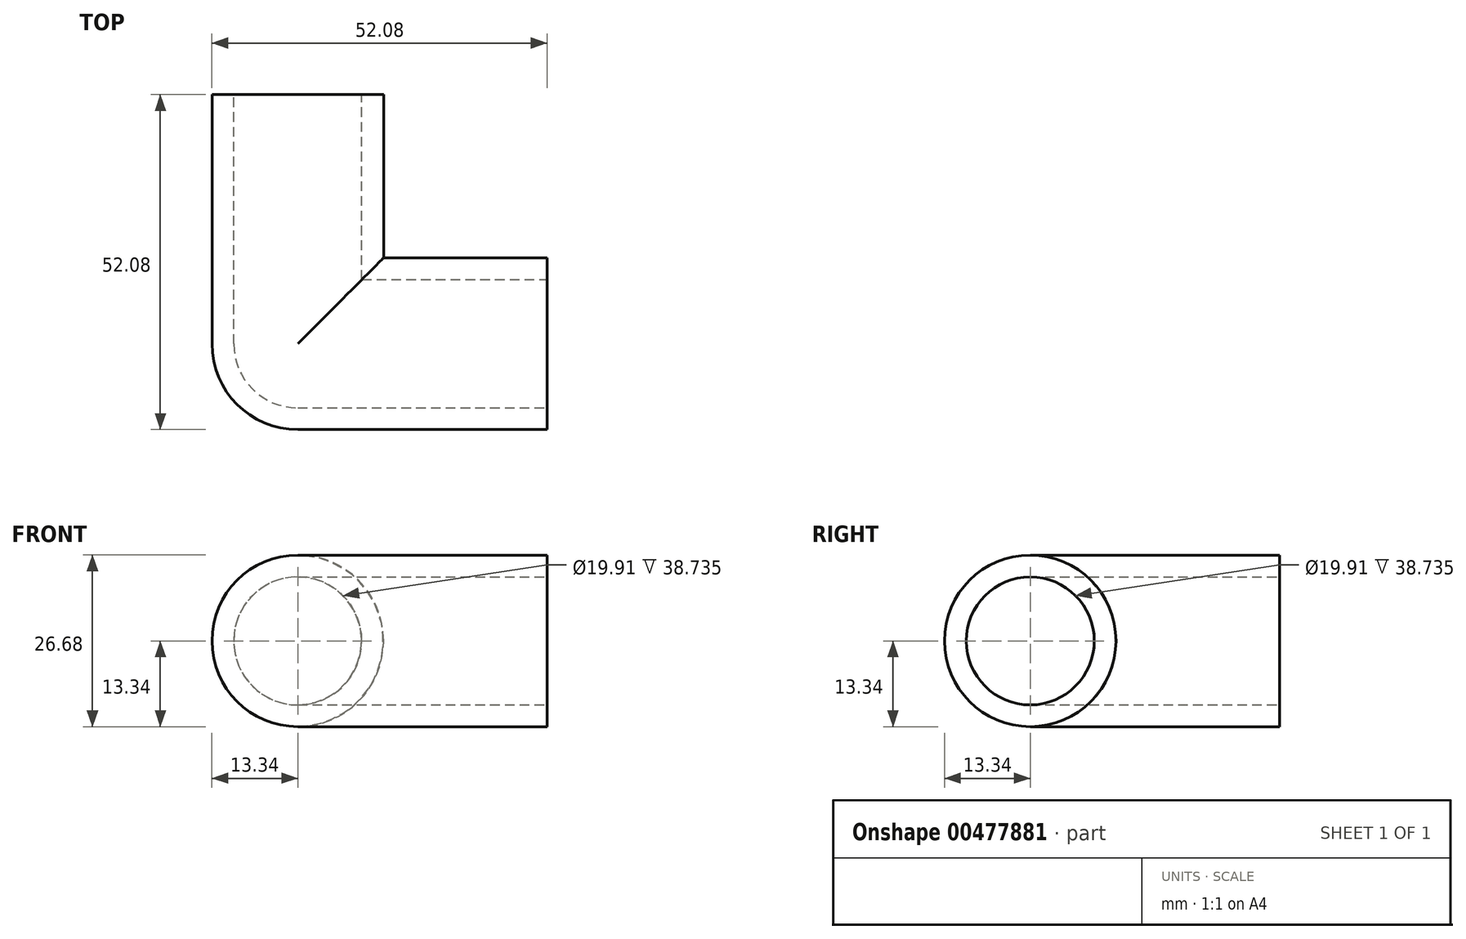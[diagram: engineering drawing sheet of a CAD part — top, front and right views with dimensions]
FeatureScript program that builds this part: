
annotation { "Feature Type Name" : "Feature", "Feature Type Description" : "" }
export const myFeature = defineFeature(function(context is Context, id is Id, definition is map)
    precondition{}
    {
        {
            var Q0;
            Q0=qCreatedBy(makeId("Top.planeOp"),FACE);
            var sketch = newSketch(context, id + "F0", { "sketchPlane" : qUnion([Q0])});
            skLineSegment(sketch, "E0", {"start": v(38.74, 13.33) * mm, "end": v(38.74, -13.33) * mm});
            skLineSegment(sketch, "E1", {"start": v(38.74, -13.34) * mm, "end": v(9.96, -13.34) * mm});
            skLineSegment(sketch, "E2", {"start": v(38.74, -9.96) * mm, "end": v(9.96, -9.96) * mm});
            skLineSegment(sketch, "E3", {"start": v(38.74, 13.33) * mm, "end": v(13.34, 13.33) * mm});
            skLineSegment(sketch, "E4", {"start": v(38.74, 9.96) * mm, "end": v(13.33, 9.96) * mm, "construction": true});
            skLineSegment(sketch, "E5", {"start": v(13.34, 38.73) * mm, "end": v(-13.33, 38.73) * mm});
            skLineSegment(sketch, "E6", {"start": v(-13.33, 38.73) * mm, "end": v(-13.33, 13.33) * mm});
            skLineSegment(sketch, "E7", {"start": v(-9.96, 38.73) * mm, "end": v(-9.96, 13.33) * mm});
            skLineSegment(sketch, "E8", {"start": v(9.96, 38.73) * mm, "end": v(9.96, 13.33) * mm, "construction": true});
            skLineSegment(sketch, "E9", {"start": v(13.34, 38.73) * mm, "end": v(13.34, 13.33) * mm});
            skLineSegment(sketch, "E10", {"start": v(26.04, 13.33) * mm, "end": v(26.03, 9.96) * mm, "construction": true});
            skLineSegment(sketch, "E11", {"start": v(24.35, -9.96) * mm, "end": v(24.35, -13.34) * mm, "construction": true});
            skLineSegment(sketch, "E12", {"start": v(-13.33, 26.03) * mm, "end": v(-9.96, 26.03) * mm, "construction": true});
            skPoint(sketch, "E12.startSnap0", {"position": v(-13.33, 26.03) * mm});
            skLineSegment(sketch, "E13", {"start": v(9.96, 26.03) * mm, "end": v(13.34, 26.03) * mm, "construction": true});
            skArc(sketch, "E14", {"start": v(13.33, 9.96) * mm, "mid": v(10.95, 10.95) * mm, "end": v(9.96, 13.33) * mm, "construction": true});
            skLineSegment(sketch, "E15", {"start": v(9.96, -13.34) * mm, "end": v(0, -13.34) * mm});
            skLineSegment(sketch, "E16", {"start": v(-13.33, 0) * mm, "end": v(-13.33, 13.33) * mm});
            skLineSegment(sketch, "E17", {"start": v(-9.96, 13.33) * mm, "end": v(-9.96, 0) * mm});
            skLineSegment(sketch, "E18", {"start": v(0, -9.96) * mm, "end": v(9.96, -9.96) * mm});
            skLineSegment(sketch, "E19", {"start": v(38.74, 0) * mm, "end": v(-9.96, 0) * mm});
            skPoint(sketch, "E19.endSnap0", {"position": v(-9.96, 1.69) * mm});
            skLineSegment(sketch, "E20", {"start": v(0, 38.73) * mm, "end": v(0, -9.96) * mm});
            skLineSegment(sketch, "E21", {"start": v(-9.96, 0) * mm, "end": v(-13.33, 0) * mm});
            skLineSegment(sketch, "E22", {"start": v(0, -9.96) * mm, "end": v(0, -13.34) * mm});
            skPoint(sketch, "E23", {"position": v(0, 0) * mm});
            skPoint(sketch, "E24.orphan", {"position": v(-13.33, -13.33) * mm});
            skPoint(sketch, "E25.start.orphan", {"position": v(-9.96, -9.96) * mm});
            skSolve(sketch);
        }
        {
            var Q0;
            {var subQ2=sQuery(id+"F0.wireOp",EDGE,"E1");Q0=makeQuery(id+"F0.imprint","IMPRINT",FACE,{"disambiguationData":[TD([[makeQuery(id+"F0.imprint","IMPRINT",EDGE,{"derivedFrom":subQ2}),-1.0]])]});}
            var Q1;
            Q1=sQuery(id+"F0.wireOp",EDGE,"E19");
            revolve(context, id + "F1", {"entities" : qUnion([Q0]), "axis" : qUnion([Q1]), "revolveType" : RevolveType.FULL});
        }
        {
            var Q0;
            {var subQ1=sQuery(id+"F0.wireOp",EDGE,"E6");Q0=makeQuery(id+"F0.imprint","IMPRINT",FACE,{"disambiguationData":[TD([[makeQuery(id+"F0.imprint","IMPRINT",EDGE,{"derivedFrom":subQ1}),1.0]])]});}
            var Q1;
            Q1=sQuery(id+"F0.wireOp",EDGE,"E20");
            revolve(context, id + "F2", {"operationType" : NewBodyOperationType.ADD, "entities" : qUnion([Q0]), "axis" : qUnion([Q1]), "revolveType" : RevolveType.FULL});
        }
        {
            var Q0;
            Q0=makeQuery(id+"F1.opRevolve","SWEPT_FACE",FACE,{"disambiguationData":[OSD([sQuery(id+"F0.wireOp",EDGE,"E0")])]});
            var sketch = newSketch(context, id + "F3", { "sketchPlane" : qUnion([Q0])});
            skSolve(sketch);
        }
        {
            var Q0;
            Q0=makeQuery(id+"F3.imprint","IMPRINT",FACE,{"disambiguationData":[TD([[makeQuery(id+"F3.imprint","IMPRINT",EDGE,{"derivedFrom":makeQuery(id+"F1.opRevolve","SWEPT_EDGE",EDGE,{"disambiguationData":[OSD([sQuery(id+"F0.wireOp",EDGE,"E0"),sQuery(id+"F0.wireOp",EDGE,"E2")])]})}),1.0]])]});
            var Q1;
            Q1=sQuery(id+"F0.wireOp",VERTEX,"E23");
            extrude(context, id + "F4", {"entities" : qUnion([Q0]), "operationType" : NewBodyOperationType.REMOVE, "endBound" : BoundingType.UP_TO_VERTEX, "oppositeDirection" : true, "endBoundEntityVertex" : qUnion([Q1]), "depth" : 25.4 * mm});
        }
        {
            var Q0;
            Q0=makeQuery(id+"F2.opRevolve","SWEPT_FACE",FACE,{"disambiguationData":[OSD([sQuery(id+"F0.wireOp",EDGE,"E5")])]});
            var sketch = newSketch(context, id + "F5", { "sketchPlane" : qUnion([Q0])});
            skSolve(sketch);
        }
        {
            var Q0;
            Q0=makeQuery(id+"F5.imprint","IMPRINT",FACE,{"disambiguationData":[TD([[makeQuery(id+"F5.imprint","IMPRINT",EDGE,{"derivedFrom":makeQuery(id+"F2.opRevolve","SWEPT_EDGE",EDGE,{"disambiguationData":[OSD([sQuery(id+"F0.wireOp",EDGE,"E5"),sQuery(id+"F0.wireOp",EDGE,"E7")])]})}),1.0]])]});
            var Q1;
            Q1=sQuery(id+"F0.wireOp",VERTEX,"E23");
            extrude(context, id + "F6", {"entities" : qUnion([Q0]), "operationType" : NewBodyOperationType.REMOVE, "endBound" : BoundingType.UP_TO_VERTEX, "oppositeDirection" : true, "endBoundEntityVertex" : qUnion([Q1]), "depth" : 25.4 * mm});
        }
        {
            var Q0;
            Q0=makeQuery(id+"F1.opRevolve","SWEPT_FACE",FACE,{"disambiguationData":[OSD([sQuery(id+"F0.wireOp",EDGE,"E22")])]});
            var Q1;
            Q1=makeQuery(id+"F2.boolean.opBoolean","INTERSECT",EDGE,{"disambiguationData":[OD(1.0)],"derivedFrom":[makeQuery(id+"F1.opRevolve","SWEPT_FACE",FACE,{"disambiguationData":[OSD([sQuery(id+"F0.wireOp",EDGE,"E22")])]}),makeQuery(id+"F2.opRevolve","SWEPT_FACE",FACE,{"disambiguationData":[OSD([sQuery(id+"F0.wireOp",EDGE,"E21")])]})]});
            revolve(context, id + "F7", {"operationType" : NewBodyOperationType.ADD, "entities" : qUnion([Q0]), "axis" : qUnion([Q1]), "revolveType" : RevolveType.ONE_DIRECTION, "oppositeDirection" : true, "angle" : 90 * degree});
        }
    });
